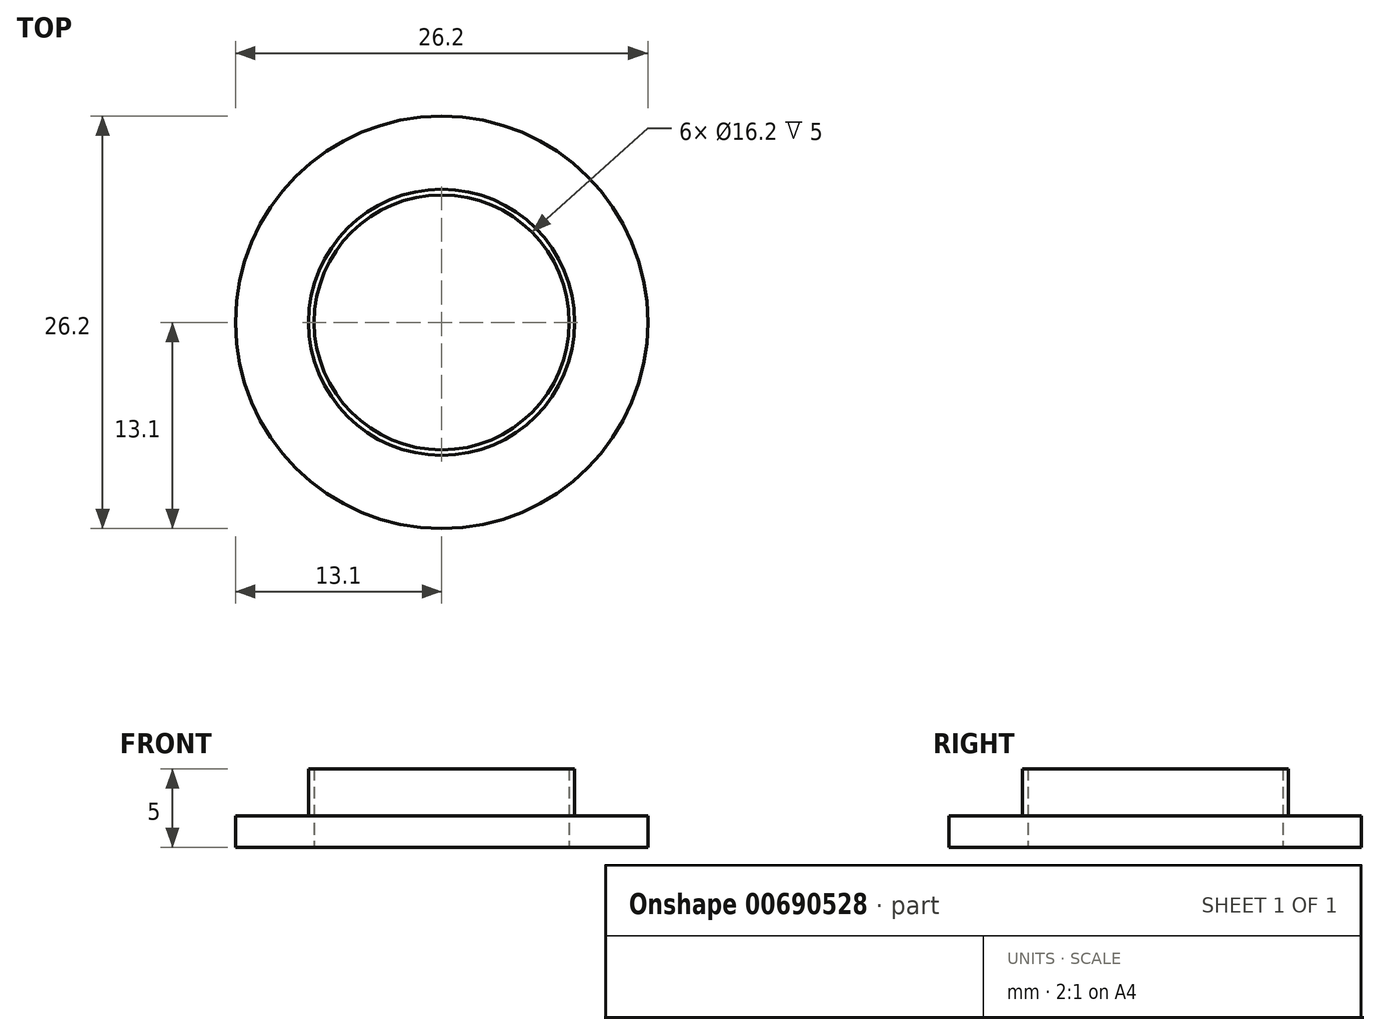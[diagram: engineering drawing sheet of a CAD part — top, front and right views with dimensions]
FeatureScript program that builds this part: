
annotation { "Feature Type Name" : "Feature", "Feature Type Description" : "" }
export const myFeature = defineFeature(function(context is Context, id is Id, definition is map)
    precondition{}
    {
        {
            var Q0;
            Q0=qCreatedBy(makeId("Front.planeOp"),FACE);
            var sketch = newSketch(context, id + "F0", { "sketchPlane" : qUnion([Q0])});
            skLineSegment(sketch, "E0", {"start": v(0, 0) * mm, "end": v(0, 7.46) * mm});
            skSolve(sketch);
        }
        {
            var Q0;
            Q0=qCreatedBy(makeId("Front.planeOp"),FACE);
            var sketch = newSketch(context, id + "F1", { "sketchPlane" : qUnion([Q0])});
            skLineSegment(sketch, "E1", {"start": v(-8.1, 0) * mm, "end": v(-8.1, 5) * mm});
            skLineSegment(sketch, "E2", {"start": v(-8.1, 5) * mm, "end": v(-8.45, 5) * mm});
            skLineSegment(sketch, "E3", {"start": v(-8.45, 5) * mm, "end": v(-8.45, 2) * mm});
            skLineSegment(sketch, "E4", {"start": v(-8.45, 2) * mm, "end": v(-13.1, 2) * mm});
            skLineSegment(sketch, "E5", {"start": v(-13.1, 2) * mm, "end": v(-13.1, 0) * mm});
            skLineSegment(sketch, "E6", {"start": v(-13.1, 0) * mm, "end": v(-8.1, 0) * mm});
            skSolve(sketch);
        }
        {
            var Q0;
            Q0=makeQuery(id+"F1.imprint","IMPRINT",FACE,{"disambiguationData":[TD([[makeQuery(id+"F1.imprint","IMPRINT",EDGE,{"derivedFrom":sQuery(id+"F1.wireOp",EDGE,"E1")}),1.0]])]});
            var Q1;
            Q1=sQuery(id+"F0.wireOp",EDGE,"E0");
            revolve(context, id + "F2", {"surfaceOperationType" : NewSurfaceOperationType.NEW, "entities" : qUnion([Q0]), "axis" : qUnion([Q1]), "revolveType" : RevolveType.FULL});
        }
    });
